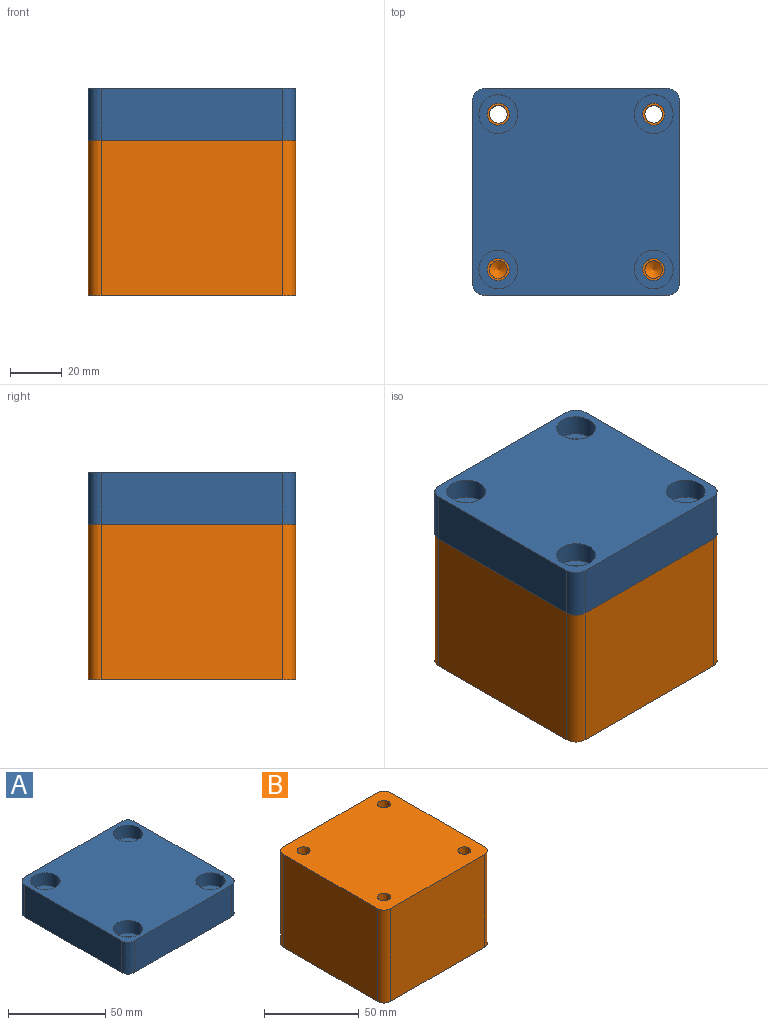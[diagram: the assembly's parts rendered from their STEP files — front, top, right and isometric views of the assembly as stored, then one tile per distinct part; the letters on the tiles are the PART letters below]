
ASSEMBLY  parts=2 mates=1
PART A: 22 faces, bbox 80x80x20 mm
  f0: plane 70x20mm, normal (0,-1,0), area 1400mm2, adj f4,f5,f18,f21
  f1: plane 70x20mm, normal (1,0,0), area 1400mm2, adj f4,f5,f18,f19
  f2: plane 70x20mm, normal (0,1,0), area 1400mm2, adj f4,f5,f19,f20
  f3: plane 70x20mm, normal (-1,0,0), area 1400mm2, adj f4,f5,f20,f21
  f4: plane 80x80mm, normal (0,0,1), area 5671.7mm2, adj f0,f1,f2,f3,f8,f11,f14,f17
  f5: plane 80x80mm, normal (0,0,-1), area 6151.6mm2, adj f0,f1,f2,f3,f6,f9,f12,f15
  f6: cylinder r=4.25mm len=12mm, axis (0,0,1), area 320.4mm2, adj f5,f7
  f7: plane 15x15mm, normal (0,0,1), area 120mm2, adj f6,f8
  f8: cylinder r=7.5mm len=15mm, axis (0,0,1), area 377mm2, adj f4,f7
  f9: cylinder r=4.25mm len=12mm, axis (0,0,1), area 320.4mm2, adj f5,f10
  f10: plane 15x15mm, normal (0,0,1), area 120mm2, adj f9,f11
  f11: cylinder r=7.5mm len=15mm, axis (0,0,1), area 377mm2, adj f4,f10
  f12: cylinder r=4.25mm len=12mm, axis (0,0,1), area 320.4mm2, adj f5,f13
  f13: plane 15x15mm, normal (0,0,1), area 120mm2, adj f12,f14
  f14: cylinder r=7.5mm len=15mm, axis (0,0,1), area 377mm2, adj f4,f13
  f15: cylinder r=4.25mm len=12mm, axis (0,0,1), area 320.4mm2, adj f5,f16
  f16: plane 15x15mm, normal (0,0,1), area 120mm2, adj f15,f17
  f17: cylinder r=7.5mm len=15mm, axis (0,0,1), area 377mm2, adj f4,f16
  f18: cylinder r=5mm len=20mm, axis (0,0,1), area 157.1mm2, adj f0,f1,f4,f5
  f19: cylinder r=5mm len=20mm, axis (0,0,-1), area 157.1mm2, adj f1,f2,f4,f5
  f20: cylinder r=5mm len=20mm, axis (0,0,1), area 157.1mm2, adj f2,f3,f4,f5
  f21: cylinder r=5mm len=20mm, axis (0,0,-1), area 157.1mm2, adj f0,f3,f4,f5
PART B: 16 faces, bbox 80x80x60 mm
  f0: plane 70x60mm, normal (0,-1,0), area 4200mm2, adj f4,f5,f12,f15
  f1: plane 70x60mm, normal (1,0,0), area 4200mm2, adj f4,f5,f12,f13
  f2: plane 70x60mm, normal (0,1,0), area 4200mm2, adj f4,f5,f13,f14
  f3: plane 70x60mm, normal (-1,0,0), area 4200mm2, adj f4,f5,f14,f15
  f4: plane 80x80mm, normal (0,0,-1), area 6305.9mm2, adj f0,f1,f2,f3,f10,f11,f12,f13
  f5: plane 80x80mm, normal (0,0,1), area 6233.3mm2, adj f0,f1,f2,f3,f7,f9,f10,f11
  f6: cone r=0mm half-angle=59deg, axis (0,0,1), area 42.4mm2, adj f7
  f7: cylinder r=3.4mm len=23.75mm, axis (0,0,1), area 507.4mm2, adj f5,f6
  f8: cone r=0mm half-angle=59deg, axis (0,0,1), area 42.4mm2, adj f9
  f9: cylinder r=3.4mm len=23.75mm, axis (0,0,1), area 507.4mm2, adj f5,f8
  f10: cylinder r=3.4mm len=60mm, axis (0,0,1), area 1281.8mm2, adj f4,f5
  f11: cylinder r=3.4mm len=60mm, axis (0,0,1), area 1281.8mm2, adj f4,f5
  f12: cylinder r=5mm len=60mm, axis (0,0,-1), area 471.2mm2, adj f0,f1,f4,f5
  f13: cylinder r=5mm len=60mm, axis (0,0,1), area 471.2mm2, adj f1,f2,f4,f5
  f14: cylinder r=5mm len=60mm, axis (0,0,-1), area 471.2mm2, adj f2,f3,f4,f5
  f15: cylinder r=5mm len=60mm, axis (0,0,1), area 471.2mm2, adj f0,f3,f4,f5
PLACE A t=(-3.62,-20.34,12.62)mm
PLACE B t=(-3.62,-20.34,12.62)mm fixed
MATE fastened B.f5 <-> A.f5  axis (0,0,1) through (-3.62,-20.34,12.62)mm
